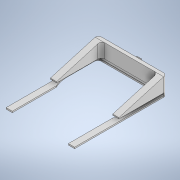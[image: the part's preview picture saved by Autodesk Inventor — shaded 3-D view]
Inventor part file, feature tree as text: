
AUTODESK INVENTOR PART (.ipt)
format: ipt  version: 2020 (Build 240168000, 168)  size: 236,032 bytes
history: native  units: in
note: dims shown in document units (in); Inventor stores cm internally (conversion verified against a paired STEP export)
features: sketch x11, extrude x9, fillet x3
ambient origin geometry x8: Origin, YZ Plane, XZ Plane, XY Plane, X Axis, Y Axis, Z Axis, Center Point
bodies: Solid1 (feature_tree)
feature tree (23):
  extrude  "Extrusion1"  Depth=3.937in
  extrude  "Extrusion2"  TaperAngle=0.0deg  [1 undecoded]
  extrude  "Extrusion7"  Depth=3.622in
  extrude  "Extrusion8"  Depth=0.2126in TaperAngle=0.0deg
  extrude  "Extrusion9"  Depth=3.5827in TaperAngle=0.0deg
  extrude  "Extrusion10"  Depth=0.1969in
  fillet  "Fillet1"  Radius=0.1969in
  fillet  "Fillet2"  Radius=0.3307in
  extrude  "Extrusion11"  Depth=0.3937in TaperAngle=0.0deg
  extrude  "Extrusion12"  Depth=0.2126in
  fillet  "Fillet5"  Radius=0.1654in
  sketch  "Sketch18"  dims[d45=0.0in d46=0.0in d47=0.0787in]
  sketch  "Sketch19"  dims[d48=4.5485in]
  extrude  "Extrusion13"  Depth=0.0787in
  sketch  "Sketch1"  dims[d0=3.937in d1=4.7244in]
  sketch  "Sketch2"  dims[d2=1.0236in d3=0.0in d9=0.0in d10=0.0in]
  sketch  "Sketch11"  dims[d23=4.5276in d24=3.622in]
  sketch  "Sketch13"  dims[d25=1.752in d26=0.2126in d27=0.0in]
  sketch  "Sketch14"  dims[d28=3.5827in d29=0.0in d30=3.5827in d31=0.0in]
  sketch  "Sketch15"  dims[d32=1.9685in d33=0.0in d34=0.1969in d35=0.1969in d38=0.3307in]
  sketch  "Sketch16"  dims[d39=0.1181in d40=0.3937in d41=0.0in]
  sketch  "Sketch17"  dims[d42=0.2126in d43=0.1654in d44=0.1654in]
  sketch  "Sketch20"  dims[d49=0.1339in d50=0.0787in d51=0.811in d52=1.9544in d53=2.5731in d54=0.748in d56=0.5906in d57=0.0in d4=0.0197in d5=0.0344in]
note: 1 required parameter value undecoded (feature->parameter linkage not recoverable at this tier; creation-order binding heuristic only, values carry confidence <= 0.55)
